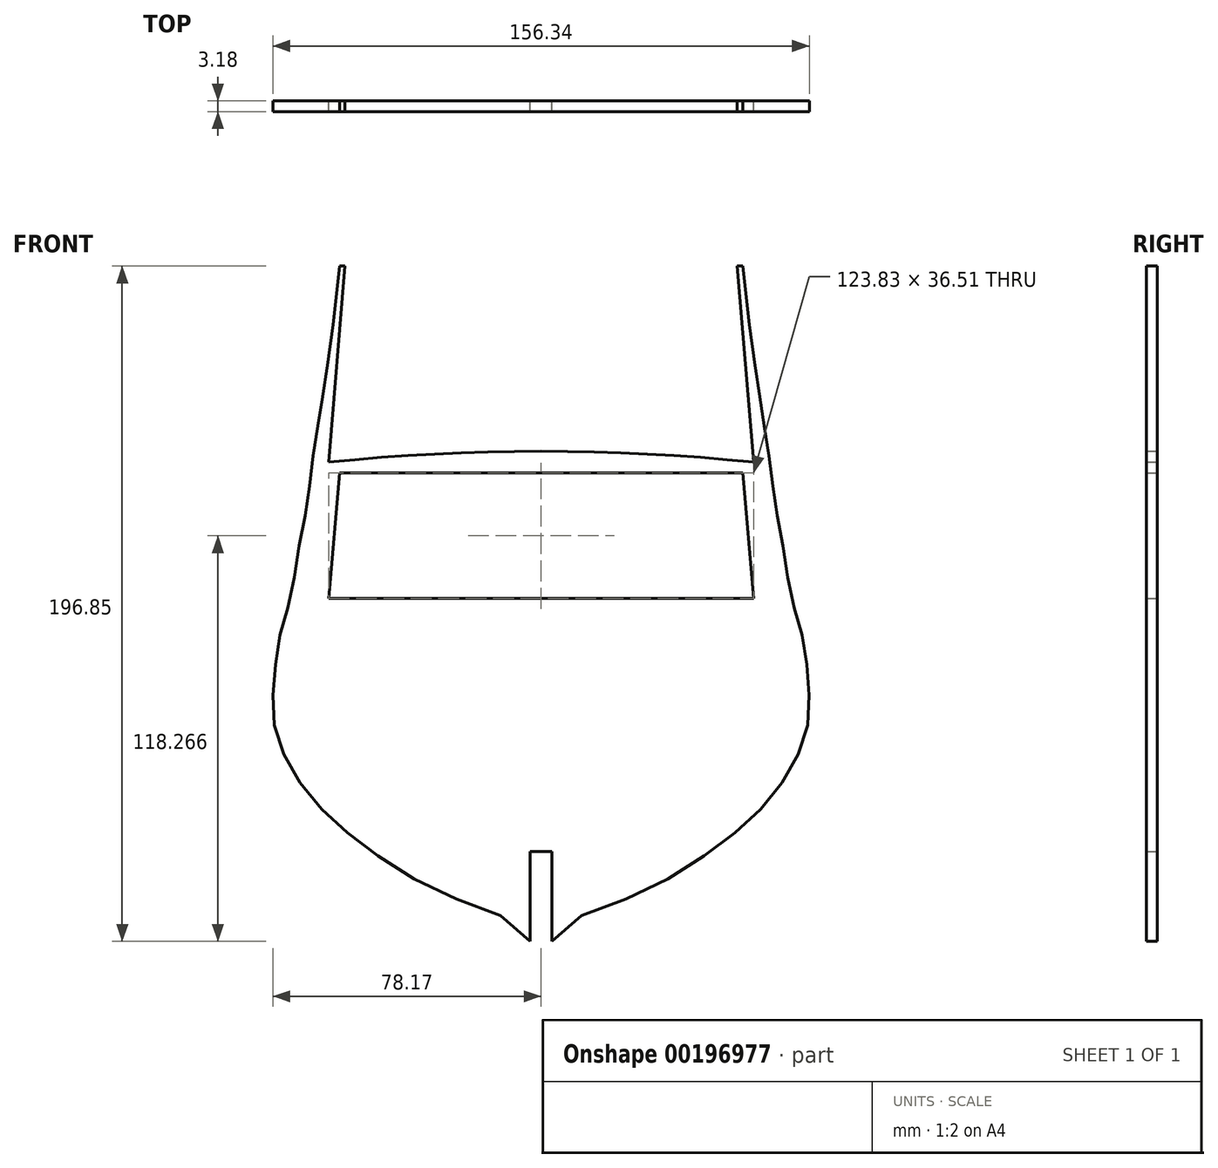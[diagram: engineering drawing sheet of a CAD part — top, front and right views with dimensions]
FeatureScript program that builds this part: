
annotation { "Feature Type Name" : "Feature", "Feature Type Description" : "" }
export const myFeature = defineFeature(function(context is Context, id is Id, definition is map)
    precondition{}
    {
        {
            var Q0;
            Q0=qCreatedBy(makeId("Front.planeOp"),FACE);
            var sketch = newSketch(context, id + "F0", { "sketchPlane" : qUnion([Q0])});
            skLineSegment(sketch, "E0", {"start": v(0, 0) * mm, "end": v(0, -100.01) * mm, "construction": true});
            skLineSegment(sketch, "E1", {"start": v(0, -100.01) * mm, "end": v(3.18, -100.01) * mm, "construction": true});
            skLineSegment(sketch, "E2", {"start": v(3.17, -100.01) * mm, "end": v(3.17, -73.82) * mm});
            skLineSegment(sketch, "E3", {"start": v(3.18, -73.82) * mm, "end": v(0, -73.82) * mm});
            skLineSegment(sketch, "E4", {"start": v(0, -73.82) * mm, "end": v(-3.18, -73.82) * mm});
            skLineSegment(sketch, "E5", {"start": v(-3.17, -73.82) * mm, "end": v(-3.17, -100.01) * mm});
            skLineSegment(sketch, "E6", {"start": v(-3.18, -100.01) * mm, "end": v(0, -100.01) * mm, "construction": true});
            skLineSegment(sketch, "E7", {"start": v(0, 0) * mm, "end": v(0, 36.51) * mm, "construction": true});
            skLineSegment(sketch, "E8", {"start": v(0, 36.51) * mm, "end": v(58.74, 36.51) * mm});
            skLineSegment(sketch, "E9", {"start": v(58.74, 36.51) * mm, "end": v(61.91, 0) * mm});
            skLineSegment(sketch, "E10", {"start": v(61.91, 0) * mm, "end": v(0, 0) * mm});
            skLineSegment(sketch, "E11", {"start": v(0, 0) * mm, "end": v(-61.91, 0) * mm});
            skLineSegment(sketch, "E12", {"start": v(-61.91, 0) * mm, "end": v(-58.74, 36.51) * mm});
            skLineSegment(sketch, "E13", {"start": v(-58.74, 36.51) * mm, "end": v(0, 36.51) * mm});
            skFitSpline(sketch, "E14", {"points": [v(3.18, -100.01) * mm, v(25.4, -87.31) * mm, v(49.21, -73.82) * mm, v(63.5, -61.91) * mm, v(73.03, -49.21) * mm, v(77.79, -36.51) * mm, v(77.79, -23.81) * mm, v(76.2, -11.11) * mm, v(73.03, 0) * mm, v(70.64, 14.29) * mm, v(68.26, 26.99) * mm, v(66.68, 39.69) * mm, v(64.7, 52.39) * mm, v(62.7, 65.09) * mm, v(58.74, 96.84) * mm], "startDerivative": vector(108.65, 237.9) * mm, "endDerivative": vector(-47.78, 477.8) * mm});
            skPoint(sketch, "E15", {"position": v(9.53, -93.66) * mm});
            skLineSegment(sketch, "E16", {"start": v(58.74, 96.84) * mm, "end": v(57.15, 96.84) * mm});
            skLineSegment(sketch, "E17", {"start": v(57.15, 96.84) * mm, "end": v(61.91, 39.69) * mm});
            skLineSegment(sketch, "E18", {"start": v(61.91, 39.69) * mm, "end": v(66.68, 39.69) * mm, "construction": true});
            skArc(sketch, "E19", {"start": v(61.91, 39.69) * mm, "mid": v(0, 42.86) * mm, "end": v(-61.91, 39.69) * mm});
            skLineSegment(sketch, "E20", {"start": v(0, 36.51) * mm, "end": v(0, 42.86) * mm, "construction": true});
            skFitSpline(sketch, "E21.MirrorCS", {"points": [v(-3.18, -100.01) * mm, v(-25.4, -87.31) * mm, v(-49.21, -73.82) * mm, v(-63.5, -61.91) * mm, v(-73.03, -49.21) * mm, v(-77.79, -36.51) * mm, v(-77.79, -23.81) * mm, v(-76.2, -11.11) * mm, v(-73.03, 0) * mm, v(-70.64, 14.29) * mm, v(-68.26, 26.99) * mm, v(-66.68, 39.69) * mm, v(-64.7, 52.39) * mm, v(-62.7, 65.09) * mm, v(-58.74, 96.84) * mm], "startDerivative": vector(-108.65, 237.9) * mm, "endDerivative": vector(47.78, 477.8) * mm});
            skLineSegment(sketch, "E22.MirrorCS", {"start": v(-57.15, 96.84) * mm, "end": v(-61.91, 39.69) * mm});
            skLineSegment(sketch, "E23.MirrorCS", {"start": v(-58.74, 96.84) * mm, "end": v(-57.15, 96.84) * mm});
            skSolve(sketch);
        }
        {
            var Q0;
            Q0=makeQuery(id+"F0.imprint","IMPRINT",FACE,{"disambiguationData":[TD([[makeQuery(id+"F0.imprint","IMPRINT",EDGE,{"derivedFrom":sQuery(id+"F0.wireOp",EDGE,"E2")}),-1.0]])]});
            extrude(context, id + "F1", {"entities" : qUnion([Q0]), "endBound" : BoundingType.SYMMETRIC, "depth" : 3.17 * mm});
        }
    });
